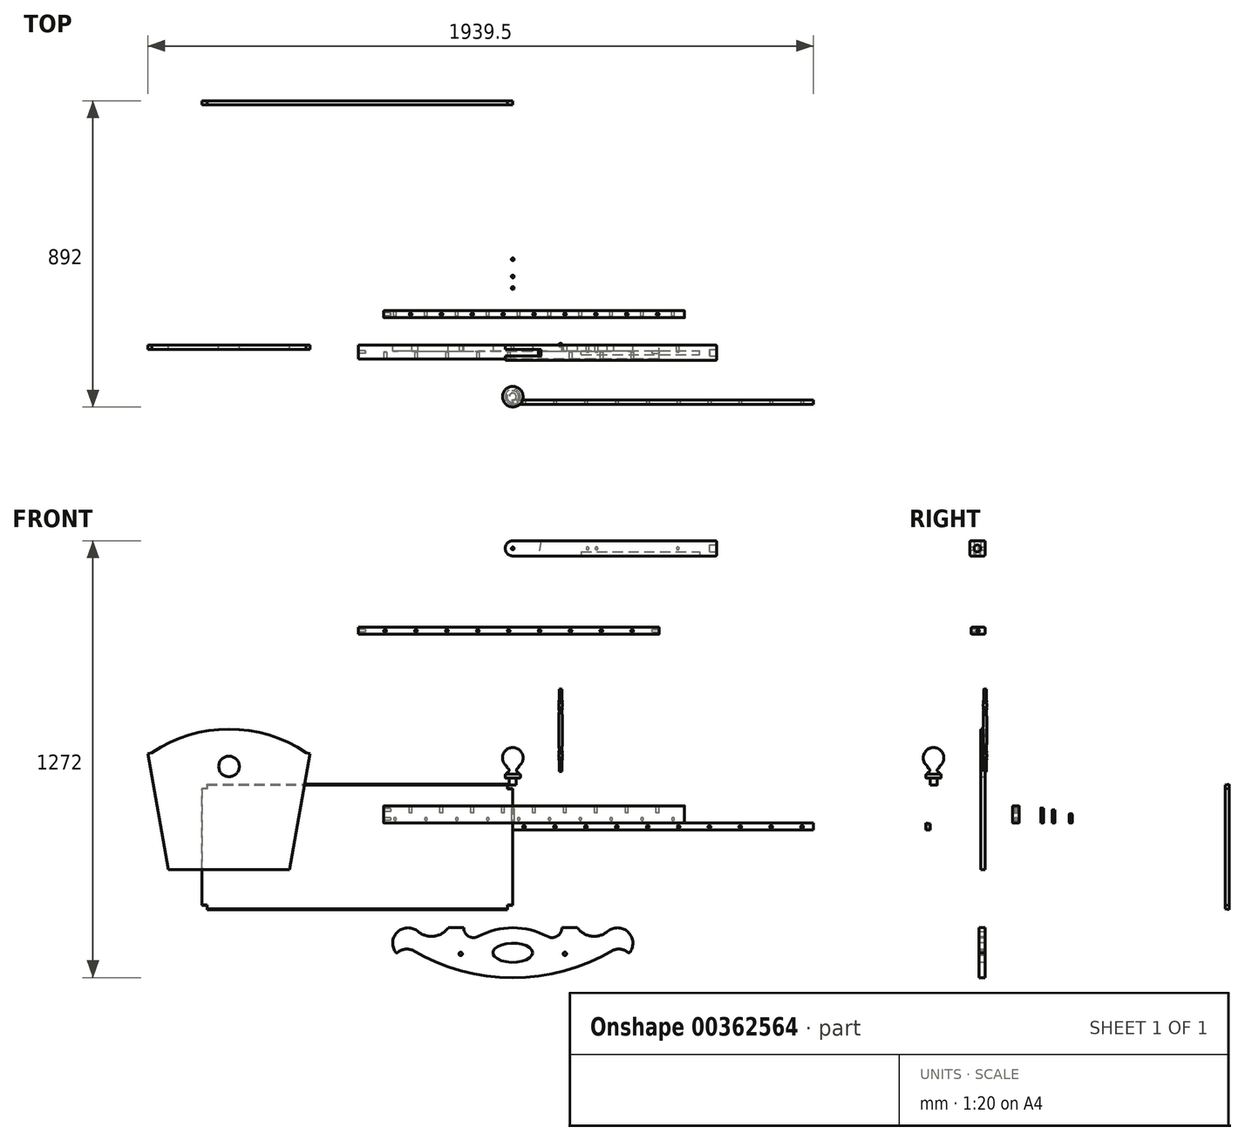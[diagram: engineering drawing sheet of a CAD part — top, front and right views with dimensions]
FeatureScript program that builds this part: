
annotation { "Feature Type Name" : "Feature", "Feature Type Description" : "" }
export const myFeature = defineFeature(function(context is Context, id is Id, definition is map)
    precondition{}
    {
        {
            var Q0;
            Q0=qCreatedBy(makeId("Top.planeOp"),FACE);
            var sketch = newSketch(context, id + "F0", { "sketchPlane" : qUnion([Q0])});
            skLineSegment(sketch, "E0.bottom", {"start": v(-376, 100) * mm, "end": v(500, 100) * mm});
            skLineSegment(sketch, "E0.top", {"start": v(-376, 80) * mm, "end": v(500, 80) * mm});
            skLineSegment(sketch, "E0.left", {"start": v(-376, 100) * mm, "end": v(-376, 80) * mm});
            skLineSegment(sketch, "E0.right", {"start": v(500, 100) * mm, "end": v(500, 80) * mm});
            skSolve(sketch);
        }
        {
            var Q0;
            Q0=makeQuery(id+"F0.imprint","IMPRINT",FACE,{"disambiguationData":[TD([[makeQuery(id+"F0.imprint","IMPRINT",EDGE,{"derivedFrom":sQuery(id+"F0.wireOp",EDGE,"E0.bottom")}),-1.0]])]});
            extrude(context, id + "F1", {"entities" : qUnion([Q0]), "depth" : 50 * mm});
        }
        {
            var Q0;
            Q0=makeQuery(id+"F1.opExtrude","SWEPT_FACE",FACE,{"disambiguationData":[OSD([sQuery(id+"F0.wireOp",EDGE,"E0.left")])]});
            var sketch = newSketch(context, id + "F2", { "sketchPlane" : qUnion([Q0])});
            skCircle(sketch, "E1", {"center": v(-90, 38) * mm, "radius": 4 * mm});
            skLineSegment(sketch, "E2", {"start": v(-90, 50) * mm, "end": v(-90, 0) * mm, "construction": true});
            skLineSegment(sketch, "E3", {"start": v(-100, 38) * mm, "end": v(-80, 38) * mm, "construction": true});
            skLineSegment(sketch, "E4", {"start": v(-100, 12) * mm, "end": v(-80, 12) * mm, "construction": true});
            skLineSegment(sketch, "E5", {"start": v(-100, 25) * mm, "end": v(-80, 25) * mm, "construction": true});
            skCircle(sketch, "E6", {"center": v(-90, 12) * mm, "radius": 4 * mm});
            skSolve(sketch);
        }
        {
            var Q0;
            Q0=makeQuery(id+"F2.imprint","IMPRINT",FACE,{"disambiguationData":[TD([[makeQuery(id+"F2.imprint","IMPRINT",EDGE,{"derivedFrom":sQuery(id+"F2.wireOp",EDGE,"E1")}),-1.0]])]});
            cPlane(context, id + "F3", {"entities" : qUnion([Q0]), "cplaneType" : CPlaneType.OFFSET, "offset" : 438 * mm, "oppositeDirection" : true, "width" : 150 * mm, "height" : 150 * mm});
        }
        {
            var Q0;
            Q0=makeQuery(id+"F2.imprint","IMPRINT",FACE,{"disambiguationData":[TD([[makeQuery(id+"F2.imprint","IMPRINT",EDGE,{"derivedFrom":sQuery(id+"F2.wireOp",EDGE,"E1")}),1.0]])]});
            var Q1;
            Q1=makeQuery(id+"F2.imprint","IMPRINT",FACE,{"disambiguationData":[TD([[makeQuery(id+"F2.imprint","IMPRINT",EDGE,{"derivedFrom":sQuery(id+"F2.wireOp",EDGE,"E6")}),1.0]])]});
            extrude(context, id + "F4", {"entities" : qUnion([Q0, Q1]), "operationType" : NewBodyOperationType.REMOVE, "oppositeDirection" : true, "depth" : 20 * mm});
        }
        {
            var Q0;
            Q0=makeQuery(id+"F1.opExtrude","CAP_FACE",FACE,{"disambiguationData":[OSD([sQuery(id+"F0.wireOp",EDGE,"E0.bottom"),sQuery(id+"F0.wireOp",EDGE,"E0.top"),sQuery(id+"F0.wireOp",EDGE,"E0.left"),sQuery(id+"F0.wireOp",EDGE,"E0.right")])],"isStart":false});
            var sketch = newSketch(context, id + "F5", { "sketchPlane" : qUnion([Q0])});
            skLineSegment(sketch, "E7", {"start": v(500, 90) * mm, "end": v(-376, 90) * mm, "construction": true});
            skCircle(sketch, "E8", {"center": v(-298, 90) * mm, "radius": 4 * mm});
            skCircle(sketch, "E9", {"center": v(-208, 90) * mm, "radius": 4 * mm});
            skCircle(sketch, "E10", {"center": v(-118, 90) * mm, "radius": 4 * mm});
            skCircle(sketch, "E11", {"center": v(-28, 90) * mm, "radius": 4 * mm});
            skCircle(sketch, "E12", {"center": v(62, 90) * mm, "radius": 4 * mm});
            skCircle(sketch, "E13", {"center": v(152, 90) * mm, "radius": 4 * mm});
            skCircle(sketch, "E14", {"center": v(242, 90) * mm, "radius": 4 * mm});
            skCircle(sketch, "E15", {"center": v(332, 90) * mm, "radius": 4 * mm});
            skCircle(sketch, "E16", {"center": v(422, 90) * mm, "radius": 4 * mm});
            skSolve(sketch);
        }
        {
            var Q0;
            Q0=makeQuery(id+"F5.imprint","IMPRINT",FACE,{"disambiguationData":[TD([[makeQuery(id+"F5.imprint","IMPRINT",EDGE,{"derivedFrom":sQuery(id+"F5.wireOp",EDGE,"E8")}),1.0]])]});
            var Q1;
            Q1=makeQuery(id+"F5.imprint","IMPRINT",FACE,{"disambiguationData":[TD([[makeQuery(id+"F5.imprint","IMPRINT",EDGE,{"derivedFrom":sQuery(id+"F5.wireOp",EDGE,"E9")}),1.0]])]});
            var Q2;
            Q2=makeQuery(id+"F5.imprint","IMPRINT",FACE,{"disambiguationData":[TD([[makeQuery(id+"F5.imprint","IMPRINT",EDGE,{"derivedFrom":sQuery(id+"F5.wireOp",EDGE,"E10")}),1.0]])]});
            var Q3;
            Q3=makeQuery(id+"F5.imprint","IMPRINT",FACE,{"disambiguationData":[TD([[makeQuery(id+"F5.imprint","IMPRINT",EDGE,{"derivedFrom":sQuery(id+"F5.wireOp",EDGE,"E11")}),1.0]])]});
            var Q4;
            Q4=makeQuery(id+"F5.imprint","IMPRINT",FACE,{"disambiguationData":[TD([[makeQuery(id+"F5.imprint","IMPRINT",EDGE,{"derivedFrom":sQuery(id+"F5.wireOp",EDGE,"E12")}),1.0]])]});
            var Q5;
            Q5=makeQuery(id+"F5.imprint","IMPRINT",FACE,{"disambiguationData":[TD([[makeQuery(id+"F5.imprint","IMPRINT",EDGE,{"derivedFrom":sQuery(id+"F5.wireOp",EDGE,"E13")}),1.0]])]});
            var Q6;
            Q6=makeQuery(id+"F5.imprint","IMPRINT",FACE,{"disambiguationData":[TD([[makeQuery(id+"F5.imprint","IMPRINT",EDGE,{"derivedFrom":sQuery(id+"F5.wireOp",EDGE,"E14")}),1.0]])]});
            var Q7;
            Q7=makeQuery(id+"F5.imprint","IMPRINT",FACE,{"disambiguationData":[TD([[makeQuery(id+"F5.imprint","IMPRINT",EDGE,{"derivedFrom":sQuery(id+"F5.wireOp",EDGE,"E15")}),1.0]])]});
            var Q8;
            Q8=makeQuery(id+"F5.imprint","IMPRINT",FACE,{"disambiguationData":[TD([[makeQuery(id+"F5.imprint","IMPRINT",EDGE,{"derivedFrom":sQuery(id+"F5.wireOp",EDGE,"E16")}),1.0]])]});
            extrude(context, id + "F6", {"entities" : qUnion([Q0, Q1, Q2, Q3, Q4, Q5, Q6, Q7, Q8]), "operationType" : NewBodyOperationType.REMOVE, "oppositeDirection" : true, "depth" : 20 * mm});
        }
        {
            var Q0;
            Q0=qCreatedBy(makeId("Front.planeOp"),FACE);
            var sketch = newSketch(context, id + "F7", { "sketchPlane" : qUnion([Q0])});
            skLineSegment(sketch, "E17", {"start": v(139.3, 390) * mm, "end": v(139.3, 150) * mm});
            skLineSegment(sketch, "E18", {"start": v(139.3, 150) * mm, "end": v(135.3, 150) * mm});
            skLineSegment(sketch, "E19", {"start": v(135.3, 150) * mm, "end": v(135.3, 170) * mm});
            skLineSegment(sketch, "E20", {"start": v(139.3, 390) * mm, "end": v(135.3, 390) * mm});
            skLineSegment(sketch, "E21", {"start": v(135.3, 390) * mm, "end": v(135.3, 370) * mm});
            skLineSegment(sketch, "E22", {"start": v(135.3, 370) * mm, "end": v(135.3, 358) * mm});
            skArc(sketch, "E23", {"start": v(135.3, 358) * mm, "mid": v(134.27, 354.5) * mm, "end": v(135.3, 351) * mm});
            skArc(sketch, "E24", {"start": v(135.3, 351) * mm, "mid": v(133.83, 343.5) * mm, "end": v(135.3, 336) * mm});
            skArc(sketch, "E25", {"start": v(135.3, 336) * mm, "mid": v(134.27, 332.5) * mm, "end": v(135.3, 329) * mm});
            skLineSegment(sketch, "E26", {"start": v(135.3, 358) * mm, "end": v(139.3, 358) * mm, "construction": true});
            skLineSegment(sketch, "E27", {"start": v(135.3, 351) * mm, "end": v(139.3, 351) * mm, "construction": true});
            skLineSegment(sketch, "E28", {"start": v(135.3, 336) * mm, "end": v(139.3, 336) * mm, "construction": true});
            skLineSegment(sketch, "E29", {"start": v(135.3, 329) * mm, "end": v(139.3, 329) * mm, "construction": true});
            skLineSegment(sketch, "E30", {"start": v(139.3, 270) * mm, "end": v(59.3, 270) * mm, "construction": true});
            skLineSegment(sketch, "E31.MirrorCS", {"start": v(135.3, 211) * mm, "end": v(139.3, 211) * mm, "construction": true});
            skArc(sketch, "E32.MirrorCS", {"start": v(135.3, 204) * mm, "mid": v(134.27, 207.5) * mm, "end": v(135.3, 211) * mm});
            skLineSegment(sketch, "E33.MirrorCS", {"start": v(135.3, 204) * mm, "end": v(139.3, 204) * mm, "construction": true});
            skArc(sketch, "E34.MirrorCS", {"start": v(135.3, 189) * mm, "mid": v(133.83, 196.5) * mm, "end": v(135.3, 204) * mm});
            skLineSegment(sketch, "E35.MirrorCS", {"start": v(135.3, 182) * mm, "end": v(139.3, 182) * mm, "construction": true});
            skLineSegment(sketch, "E36.MirrorCS", {"start": v(135.3, 189) * mm, "end": v(139.3, 189) * mm, "construction": true});
            skArc(sketch, "E37.MirrorCS", {"start": v(135.3, 182) * mm, "mid": v(134.27, 185.5) * mm, "end": v(135.3, 189) * mm});
            skLineSegment(sketch, "E38.MirrorCS", {"start": v(135.3, 170) * mm, "end": v(135.3, 182) * mm});
            skArc(sketch, "E39", {"start": v(135.3, 329) * mm, "mid": v(133.84, 270) * mm, "end": v(135.3, 211) * mm});
            skSolve(sketch);
        }
        {
            var Q0;
            Q0=makeQuery(id+"F7.imprint","IMPRINT",FACE,{"disambiguationData":[TD([[makeQuery(id+"F7.imprint","IMPRINT",EDGE,{"derivedFrom":sQuery(id+"F7.wireOp",EDGE,"E17")}),-1.0]])]});
            var Q1;
            Q1=sQuery(id+"F7.wireOp",EDGE,"E17");
            revolve(context, id + "F8", {"entities" : qUnion([Q0]), "axis" : qUnion([Q1]), "revolveType" : RevolveType.FULL});
        }
        {
            var Q0;
            Q0=qCreatedBy(makeId("Right.planeOp"),FACE);
            var sketch = newSketch(context, id + "F9", { "sketchPlane" : qUnion([Q0])});
            skLineSegment(sketch, "E40", {"start": v(-150, 220) * mm, "end": v(-150, 100) * mm, "construction": true});
            skLineSegment(sketch, "E41", {"start": v(-150, 220) * mm, "end": v(-150, 110.72) * mm});
            skArc(sketch, "E42", {"start": v(-150, 220) * mm, "mid": v(-178.65, 198.9) * mm, "end": v(-167, 165.28) * mm});
            skLineSegment(sketch, "E43", {"start": v(-150, 110.72) * mm, "end": v(-160, 110.72) * mm});
            skLineSegment(sketch, "E44", {"start": v(-160, 110.72) * mm, "end": v(-160, 130.72) * mm});
            skLineSegment(sketch, "E45", {"start": v(-167, 160.28) * mm, "end": v(-167, 165.28) * mm});
            skPoint(sketch, "E46", {"position": v(-167, 154) * mm});
            skArc(sketch, "E47", {"start": v(-167, 147.72) * mm, "mid": v(-160.72, 154) * mm, "end": v(-167, 160.28) * mm});
            skLineSegment(sketch, "E48", {"start": v(-167, 147.72) * mm, "end": v(-167, 142.72) * mm});
            skLineSegment(sketch, "E49", {"start": v(-167, 142.72) * mm, "end": v(-172, 142.72) * mm});
            skLineSegment(sketch, "E50", {"start": v(-172, 142.72) * mm, "end": v(-172, 130.72) * mm});
            skLineSegment(sketch, "E51", {"start": v(-172, 130.72) * mm, "end": v(-160, 130.72) * mm});
            skSolve(sketch);
        }
        {
            var Q0;
            Q0=makeQuery(id+"F9.imprint","IMPRINT",FACE,{"disambiguationData":[TD([[makeQuery(id+"F9.imprint","IMPRINT",EDGE,{"derivedFrom":sQuery(id+"F9.wireOp",EDGE,"E41")}),-1.0]])]});
            var Q1;
            Q1=sQuery(id+"F9.wireOp",EDGE,"E41");
            revolve(context, id + "F10", {"entities" : qUnion([Q0]), "axis" : qUnion([Q1]), "revolveType" : RevolveType.FULL});
        }
        {
            var Q0;
            Q0=qCreatedBy(makeId("Front.planeOp"),FACE);
            var sketch = newSketch(context, id + "F11", { "sketchPlane" : qUnion([Q0])});
            skLineSegment(sketch, "E52", {"start": v(0, -250) * mm, "end": v(0, -450) * mm, "construction": true});
            skArc(sketch, "E53", {"start": v(-275.48, -316.04) * mm, "mid": v(-337.05, -318.41) * mm, "end": v(-338.53, -380.02) * mm});
            skArc(sketch, "E54", {"start": v(-275.48, -316.04) * mm, "mid": v(-229.47, -329.53) * mm, "end": v(-188.27, -305) * mm});
            skArc(sketch, "E55.trimOffspring", {"start": v(-294.24, -369.82) * mm, "mid": v(-317.97, -368.02) * mm, "end": v(-338.53, -380.02) * mm});
            skLineSegment(sketch, "E56", {"start": v(-188.27, -305) * mm, "end": v(-143, -305) * mm});
            skArc(sketch, "E57", {"start": v(-294.24, -369.82) * mm, "mid": v(-152.48, -429.6) * mm, "end": v(0, -450) * mm});
            skArc(sketch, "E58", {"start": v(-143, -305) * mm, "mid": v(-129.19, -329.42) * mm, "end": v(-101.14, -330.17) * mm});
            skArc(sketch, "E59", {"start": v(0, -305) * mm, "mid": v(-52.11, -311.39) * mm, "end": v(-101.14, -330.17) * mm});
            skLineSegment(sketch, "E60.MirrorCS", {"start": v(188.27, -305) * mm, "end": v(143, -305) * mm});
            skArc(sketch, "E61.MirrorCS", {"start": v(294.24, -369.82) * mm, "mid": v(152.48, -429.6) * mm, "end": v(0, -450) * mm});
            skArc(sketch, "E62.MirrorCS", {"start": v(0, -305) * mm, "mid": v(52.11, -311.39) * mm, "end": v(101.14, -330.17) * mm});
            skArc(sketch, "E63.MirrorCS", {"start": v(294.24, -369.82) * mm, "mid": v(317.97, -368.02) * mm, "end": v(338.53, -380.02) * mm});
            skArc(sketch, "E64.MirrorCS", {"start": v(143, -305) * mm, "mid": v(129.19, -329.42) * mm, "end": v(101.14, -330.17) * mm});
            skArc(sketch, "E65.MirrorCS", {"start": v(275.48, -316.04) * mm, "mid": v(229.47, -329.53) * mm, "end": v(188.27, -305) * mm});
            skArc(sketch, "E66.MirrorCS", {"start": v(275.48, -316.04) * mm, "mid": v(337.05, -318.41) * mm, "end": v(338.53, -380.02) * mm});
            skSolve(sketch);
        }
        {
            var Q0;
            Q0=makeQuery(id+"F11.imprint","IMPRINT",FACE,{"disambiguationData":[TD([[makeQuery(id+"F11.imprint","IMPRINT",EDGE,{"derivedFrom":sQuery(id+"F11.wireOp",EDGE,"E53")}),1.0]])]});
            extrude(context, id + "F12", {"entities" : qUnion([Q0]), "depth" : 18 * mm});
        }
        {
            var Q0;
            Q0=makeQuery(id+"F12.opExtrude","SWEPT_EDGE",EDGE,{"disambiguationData":[OSD([sQuery(id+"F11.wireOp",EDGE,"E53"),sQuery(id+"F11.wireOp",EDGE,"E55.trimOffspring")])]});
            var Q1;
            Q1=makeQuery(id+"F12.opExtrude","SWEPT_EDGE",EDGE,{"disambiguationData":[OSD([sQuery(id+"F11.wireOp",EDGE,"E63.MirrorCS"),sQuery(id+"F11.wireOp",EDGE,"E66.MirrorCS")])]});
            fillet(context, id + "F13", {"entities" : qUnion([Q0, Q1]), "radius" : 5 * mm, "tangentPropagation" : true, "allowEdgeOverflow" : false});
        }
        {
            var Q0;
            Q0=makeQuery(id+"F12.opExtrude","CAP_FACE",FACE,{"disambiguationData":[OSD([sQuery(id+"F11.wireOp",EDGE,"E53"),sQuery(id+"F11.wireOp",EDGE,"E54"),sQuery(id+"F11.wireOp",EDGE,"E55.trimOffspring"),sQuery(id+"F11.wireOp",EDGE,"E56"),sQuery(id+"F11.wireOp",EDGE,"E57"),sQuery(id+"F11.wireOp",EDGE,"E58"),sQuery(id+"F11.wireOp",EDGE,"E59"),sQuery(id+"F11.wireOp",EDGE,"E60.MirrorCS"),sQuery(id+"F11.wireOp",EDGE,"E61.MirrorCS"),sQuery(id+"F11.wireOp",EDGE,"E62.MirrorCS"),sQuery(id+"F11.wireOp",EDGE,"E63.MirrorCS"),sQuery(id+"F11.wireOp",EDGE,"E64.MirrorCS"),sQuery(id+"F11.wireOp",EDGE,"E65.MirrorCS"),sQuery(id+"F11.wireOp",EDGE,"E66.MirrorCS")])],"isStart":false});
            var sketch = newSketch(context, id + "F14", { "sketchPlane" : qUnion([Q0])});
            skEllipse(sketch, "E67", {"center": v(0, -377.5) * mm, "majorRadius": 58 * mm, "minorRadius": 28 * mm, "majorAxis": v(1, 0)});
            skLineSegment(sketch, "E68", {"start": v(0, -305) * mm, "end": v(0, -450) * mm, "construction": true});
            skLineSegment(sketch, "E69", {"start": v(-58, -377.5) * mm, "end": v(58, -377.5) * mm, "construction": true});
            skCircle(sketch, "E70", {"center": v(-151.88, -381) * mm, "radius": 5 * mm});
            skCircle(sketch, "E71", {"center": v(151.88, -381) * mm, "radius": 5 * mm});
            skLineSegment(sketch, "E72", {"start": v(-151.88, -381) * mm, "end": v(151.88, -381) * mm, "construction": true});
            skSolve(sketch);
        }
        {
            var Q0;
            Q0=makeQuery(id+"F14.imprint","IMPRINT",FACE,{"disambiguationData":[TD([[makeQuery(id+"F14.imprint","IMPRINT",EDGE,{"derivedFrom":sQuery(id+"F14.wireOp",EDGE,"E70")}),1.0]])]});
            var Q1;
            Q1=makeQuery(id+"F14.imprint","IMPRINT",FACE,{"disambiguationData":[TD([[makeQuery(id+"F14.imprint","IMPRINT",EDGE,{"derivedFrom":sQuery(id+"F14.wireOp",EDGE,"E67")}),1.0]])]});
            var Q2;
            Q2=makeQuery(id+"F14.imprint","IMPRINT",FACE,{"disambiguationData":[TD([[makeQuery(id+"F14.imprint","IMPRINT",EDGE,{"derivedFrom":sQuery(id+"F14.wireOp",EDGE,"E71")}),1.0]])]});
            extrude(context, id + "F15", {"entities" : qUnion([Q0, Q1, Q2]), "operationType" : NewBodyOperationType.REMOVE, "endBound" : BoundingType.UP_TO_NEXT, "oppositeDirection" : true, "depth" : 25 * mm});
        }
        {
            var Q0;
            Q0=qCreatedBy(makeId("Front.planeOp"),FACE);
            var sketch = newSketch(context, id + "F16", { "sketchPlane" : qUnion([Q0])});
            skLineSegment(sketch, "E73", {"start": v(-650, -135) * mm, "end": v(-1004, -135) * mm});
            skLineSegment(sketch, "E74", {"start": v(-1004, -135) * mm, "end": v(-1063.5, 202.44) * mm});
            skLineSegment(sketch, "E75", {"start": v(-650, -135) * mm, "end": v(-590.5, 202.44) * mm});
            skLineSegment(sketch, "E76", {"start": v(-1063.5, 202.44) * mm, "end": v(-1051.68, 204.53) * mm});
            skLineSegment(sketch, "E77", {"start": v(-590.5, 202.44) * mm, "end": v(-602.32, 204.53) * mm});
            skArc(sketch, "E78", {"start": v(-602.32, 204.53) * mm, "mid": v(-827, 273.6) * mm, "end": v(-1051.68, 204.53) * mm});
            skLineSegment(sketch, "E79", {"start": v(-827, 273.6) * mm, "end": v(-827, -135) * mm, "construction": true});
            skCircle(sketch, "E80", {"center": v(-827, 165) * mm, "radius": 30 * mm});
            skSolve(sketch);
        }
        {
            var Q0;
            Q0=makeQuery(id+"F16.imprint","IMPRINT",FACE,{"disambiguationData":[TD([[makeQuery(id+"F16.imprint","IMPRINT",EDGE,{"derivedFrom":sQuery(id+"F16.wireOp",EDGE,"E73")}),-1.0]])]});
            extrude(context, id + "F17", {"entities" : qUnion([Q0]), "depth" : 12 * mm});
        }
        {
            var Q0;
            Q0=qCreatedBy(makeId("Front.planeOp"),FACE);
            var sketch = newSketch(context, id + "F18", { "sketchPlane" : qUnion([Q0])});
            skLineSegment(sketch, "E81", {"start": v(-450, 570) * mm, "end": v(426, 570) * mm});
            skLineSegment(sketch, "E82", {"start": v(426, 570) * mm, "end": v(426, 550) * mm});
            skLineSegment(sketch, "E83", {"start": v(426, 550) * mm, "end": v(-450, 550) * mm});
            skLineSegment(sketch, "E84", {"start": v(-450, 550) * mm, "end": v(-450, 570) * mm});
            skSolve(sketch);
        }
        {
            var Q0;
            Q0=makeQuery(id+"F18.imprint","IMPRINT",FACE,{"disambiguationData":[TD([[makeQuery(id+"F18.imprint","IMPRINT",EDGE,{"derivedFrom":sQuery(id+"F18.wireOp",EDGE,"E81")}),-1.0]])]});
            extrude(context, id + "F19", {"entities" : qUnion([Q0]), "depth" : 40 * mm});
        }
        {
            var Q0;
            Q0=makeQuery(id+"F19.opExtrude","CAP_FACE",FACE,{"disambiguationData":[OSD([sQuery(id+"F18.wireOp",EDGE,"E81"),sQuery(id+"F18.wireOp",EDGE,"E82"),sQuery(id+"F18.wireOp",EDGE,"E83"),sQuery(id+"F18.wireOp",EDGE,"E84")])],"isStart":false});
            var sketch = newSketch(context, id + "F20", { "sketchPlane" : qUnion([Q0])});
            skLineSegment(sketch, "E85", {"start": v(-450, 560) * mm, "end": v(426, 560) * mm, "construction": true});
            skCircle(sketch, "E86", {"center": v(348, 560) * mm, "radius": 4 * mm});
            skCircle(sketch, "E87", {"center": v(258, 560) * mm, "radius": 4 * mm});
            skCircle(sketch, "E88", {"center": v(168, 560) * mm, "radius": 4 * mm});
            skCircle(sketch, "E89", {"center": v(78, 560) * mm, "radius": 4 * mm});
            skCircle(sketch, "E90", {"center": v(-12, 560) * mm, "radius": 4 * mm});
            skCircle(sketch, "E91", {"center": v(-102, 560) * mm, "radius": 4 * mm});
            skCircle(sketch, "E92", {"center": v(-192, 560) * mm, "radius": 4 * mm});
            skCircle(sketch, "E93", {"center": v(-282, 560) * mm, "radius": 4 * mm});
            skCircle(sketch, "E94", {"center": v(-372, 560) * mm, "radius": 4 * mm});
            skSolve(sketch);
        }
        {
            var Q0;
            Q0=makeQuery(id+"F20.imprint","IMPRINT",FACE,{"disambiguationData":[TD([[makeQuery(id+"F20.imprint","IMPRINT",EDGE,{"derivedFrom":sQuery(id+"F20.wireOp",EDGE,"E94")}),1.0]])]});
            var Q1;
            Q1=makeQuery(id+"F20.imprint","IMPRINT",FACE,{"disambiguationData":[TD([[makeQuery(id+"F20.imprint","IMPRINT",EDGE,{"derivedFrom":sQuery(id+"F20.wireOp",EDGE,"E93")}),1.0]])]});
            var Q2;
            Q2=makeQuery(id+"F20.imprint","IMPRINT",FACE,{"disambiguationData":[TD([[makeQuery(id+"F20.imprint","IMPRINT",EDGE,{"derivedFrom":sQuery(id+"F20.wireOp",EDGE,"E92")}),1.0]])]});
            var Q3;
            Q3=makeQuery(id+"F20.imprint","IMPRINT",FACE,{"disambiguationData":[TD([[makeQuery(id+"F20.imprint","IMPRINT",EDGE,{"derivedFrom":sQuery(id+"F20.wireOp",EDGE,"E91")}),1.0]])]});
            var Q4;
            Q4=makeQuery(id+"F20.imprint","IMPRINT",FACE,{"disambiguationData":[TD([[makeQuery(id+"F20.imprint","IMPRINT",EDGE,{"derivedFrom":sQuery(id+"F20.wireOp",EDGE,"E90")}),1.0]])]});
            var Q5;
            Q5=makeQuery(id+"F20.imprint","IMPRINT",FACE,{"disambiguationData":[TD([[makeQuery(id+"F20.imprint","IMPRINT",EDGE,{"derivedFrom":sQuery(id+"F20.wireOp",EDGE,"E89")}),1.0]])]});
            var Q6;
            Q6=makeQuery(id+"F20.imprint","IMPRINT",FACE,{"disambiguationData":[TD([[makeQuery(id+"F20.imprint","IMPRINT",EDGE,{"derivedFrom":sQuery(id+"F20.wireOp",EDGE,"E88")}),1.0]])]});
            var Q7;
            Q7=makeQuery(id+"F20.imprint","IMPRINT",FACE,{"disambiguationData":[TD([[makeQuery(id+"F20.imprint","IMPRINT",EDGE,{"derivedFrom":sQuery(id+"F20.wireOp",EDGE,"E86")}),1.0]])]});
            var Q8;
            Q8=makeQuery(id+"F20.imprint","IMPRINT",FACE,{"disambiguationData":[TD([[makeQuery(id+"F20.imprint","IMPRINT",EDGE,{"derivedFrom":sQuery(id+"F20.wireOp",EDGE,"E87")}),1.0]])]});
            extrude(context, id + "F21", {"entities" : qUnion([Q0, Q1, Q2, Q3, Q4, Q5, Q6, Q7, Q8]), "operationType" : NewBodyOperationType.REMOVE, "oppositeDirection" : true, "depth" : 20 * mm});
        }
        {
            var Q0;
            Q0=makeQuery(id+"F19.opExtrude","SWEPT_FACE",FACE,{"disambiguationData":[OSD([sQuery(id+"F18.wireOp",EDGE,"E82")])]});
            var sketch = newSketch(context, id + "F22", { "sketchPlane" : qUnion([Q0])});
            skLineSegment(sketch, "E95", {"start": v(-20, 570) * mm, "end": v(-20, 550) * mm, "construction": true});
            skLineSegment(sketch, "E96", {"start": v(-40, 560) * mm, "end": v(0, 560) * mm, "construction": true});
            skCircle(sketch, "E97", {"center": v(-20, 560) * mm, "radius": 4 * mm});
            skSolve(sketch);
        }
        {
            var Q0;
            Q0=makeQuery(id+"F22.imprint","IMPRINT",FACE,{"disambiguationData":[TD([[makeQuery(id+"F22.imprint","IMPRINT",EDGE,{"derivedFrom":sQuery(id+"F22.wireOp",EDGE,"E97")}),1.0]])]});
            extrude(context, id + "F23", {"entities" : qUnion([Q0]), "operationType" : NewBodyOperationType.REMOVE, "oppositeDirection" : true, "depth" : 20 * mm});
        }
        {
            var Q0;
            Q0=makeQuery(id+"F19.opExtrude","SWEPT_FACE",FACE,{"disambiguationData":[OSD([sQuery(id+"F18.wireOp",EDGE,"E84")])]});
            var sketch = newSketch(context, id + "F24", { "sketchPlane" : qUnion([Q0])});
            skLineSegment(sketch, "E98", {"start": v(20, 570) * mm, "end": v(20, 550) * mm, "construction": true});
            skLineSegment(sketch, "E99", {"start": v(0, 560) * mm, "end": v(40, 560) * mm, "construction": true});
            skCircle(sketch, "E100", {"center": v(20, 560) * mm, "radius": 4 * mm});
            skSolve(sketch);
        }
        {
            var Q0;
            Q0=makeQuery(id+"F24.imprint","IMPRINT",FACE,{"disambiguationData":[TD([[makeQuery(id+"F24.imprint","IMPRINT",EDGE,{"derivedFrom":sQuery(id+"F24.wireOp",EDGE,"E100")}),1.0]])]});
            extrude(context, id + "F25", {"entities" : qUnion([Q0]), "operationType" : NewBodyOperationType.REMOVE, "oppositeDirection" : true, "depth" : 20 * mm});
        }
        {
            var Q0;
            Q0=makeQuery(id+"F19.opExtrude","CAP_EDGE",EDGE,{"disambiguationData":[OSD([sQuery(id+"F18.wireOp",EDGE,"E83")])],"isStart":false});
            var Q1;
            Q1=makeQuery(id+"F19.opExtrude","CAP_EDGE",EDGE,{"disambiguationData":[OSD([sQuery(id+"F18.wireOp",EDGE,"E83")])],"isStart":true});
            var Q2;
            Q2=makeQuery(id+"F19.opExtrude","CAP_EDGE",EDGE,{"disambiguationData":[OSD([sQuery(id+"F18.wireOp",EDGE,"E81")])],"isStart":false});
            var Q3;
            Q3=makeQuery(id+"F19.opExtrude","CAP_EDGE",EDGE,{"disambiguationData":[OSD([sQuery(id+"F18.wireOp",EDGE,"E81")])],"isStart":true});
            fillet(context, id + "F26", {"entities" : qUnion([Q0, Q1, Q2, Q3]), "radius" : 2 * mm, "tangentPropagation" : true, "allowEdgeOverflow" : false});
        }
        {
            var Q0;
            Q0=makeQuery(id+"F1.opExtrude","CAP_EDGE",EDGE,{"disambiguationData":[OSD([sQuery(id+"F0.wireOp",EDGE,"E0.top")])],"isStart":false});
            var Q1;
            Q1=makeQuery(id+"F1.opExtrude","CAP_EDGE",EDGE,{"disambiguationData":[OSD([sQuery(id+"F0.wireOp",EDGE,"E0.bottom")])],"isStart":false});
            var Q2;
            Q2=makeQuery(id+"F1.opExtrude","CAP_EDGE",EDGE,{"disambiguationData":[OSD([sQuery(id+"F0.wireOp",EDGE,"E0.top")])],"isStart":true});
            var Q3;
            Q3=makeQuery(id+"F1.opExtrude","CAP_EDGE",EDGE,{"disambiguationData":[OSD([sQuery(id+"F0.wireOp",EDGE,"E0.bottom")])],"isStart":true});
            fillet(context, id + "F27", {"entities" : qUnion([Q0, Q1, Q2, Q3]), "radius" : 2 * mm, "tangentPropagation" : true, "allowEdgeOverflow" : false});
        }
        {
            var Q0;
            Q0=makeQuery(id+"F1.opExtrude","SWEPT_FACE",FACE,{"disambiguationData":[OSD([sQuery(id+"F0.wireOp",EDGE,"E0.bottom")])]});
            var sketch = newSketch(context, id + "F28", { "sketchPlane" : qUnion([Q0])});
            skLineSegment(sketch, "E101", {"start": v(-500, 12) * mm, "end": v(376, 12) * mm, "construction": true});
            skCircle(sketch, "E102", {"center": v(-467, 12) * mm, "radius": 4 * mm});
            skCircle(sketch, "E103.1.0.0", {"center": v(-377, 12) * mm, "radius": 4 * mm});
            skCircle(sketch, "E103.2.0.0", {"center": v(-287, 12) * mm, "radius": 4 * mm});
            skCircle(sketch, "E103.3.0.0", {"center": v(-197, 12) * mm, "radius": 4 * mm});
            skCircle(sketch, "E103.4.0.0", {"center": v(-107, 12) * mm, "radius": 4 * mm});
            skCircle(sketch, "E103.5.0.0", {"center": v(-17, 12) * mm, "radius": 4 * mm});
            skCircle(sketch, "E103.6.0.0", {"center": v(73, 12) * mm, "radius": 4 * mm});
            skCircle(sketch, "E103.7.0.0", {"center": v(163, 12) * mm, "radius": 4 * mm});
            skCircle(sketch, "E103.8.0.0", {"center": v(253, 12) * mm, "radius": 4 * mm});
            skCircle(sketch, "E103.9.0.0", {"center": v(343, 12) * mm, "radius": 4 * mm});
            skLineSegment(sketch, "E103.direction1", {"start": v(-467, 12) * mm, "end": v(-377, 12) * mm, "construction": true});
            skSolve(sketch);
        }
        {
            var Q0;
            Q0=makeQuery(id+"F28.imprint","IMPRINT",FACE,{"disambiguationData":[TD([[makeQuery(id+"F28.imprint","IMPRINT",EDGE,{"derivedFrom":sQuery(id+"F28.wireOp",EDGE,"E102")}),1.0]])]});
            var Q1;
            Q1=makeQuery(id+"F28.imprint","IMPRINT",FACE,{"disambiguationData":[TD([[makeQuery(id+"F28.imprint","IMPRINT",EDGE,{"derivedFrom":sQuery(id+"F28.wireOp",EDGE,"E103.1.0.0")}),1.0]])]});
            var Q2;
            Q2=makeQuery(id+"F28.imprint","IMPRINT",FACE,{"disambiguationData":[TD([[makeQuery(id+"F28.imprint","IMPRINT",EDGE,{"derivedFrom":sQuery(id+"F28.wireOp",EDGE,"E103.2.0.0")}),1.0]])]});
            var Q3;
            Q3=makeQuery(id+"F28.imprint","IMPRINT",FACE,{"disambiguationData":[TD([[makeQuery(id+"F28.imprint","IMPRINT",EDGE,{"derivedFrom":sQuery(id+"F28.wireOp",EDGE,"E103.3.0.0")}),1.0]])]});
            var Q4;
            Q4=makeQuery(id+"F28.imprint","IMPRINT",FACE,{"disambiguationData":[TD([[makeQuery(id+"F28.imprint","IMPRINT",EDGE,{"derivedFrom":sQuery(id+"F28.wireOp",EDGE,"E103.4.0.0")}),1.0]])]});
            var Q5;
            Q5=makeQuery(id+"F28.imprint","IMPRINT",FACE,{"disambiguationData":[TD([[makeQuery(id+"F28.imprint","IMPRINT",EDGE,{"derivedFrom":sQuery(id+"F28.wireOp",EDGE,"E103.5.0.0")}),1.0]])]});
            var Q6;
            Q6=makeQuery(id+"F28.imprint","IMPRINT",FACE,{"disambiguationData":[TD([[makeQuery(id+"F28.imprint","IMPRINT",EDGE,{"derivedFrom":sQuery(id+"F28.wireOp",EDGE,"E103.6.0.0")}),1.0]])]});
            var Q7;
            Q7=makeQuery(id+"F28.imprint","IMPRINT",FACE,{"disambiguationData":[TD([[makeQuery(id+"F28.imprint","IMPRINT",EDGE,{"derivedFrom":sQuery(id+"F28.wireOp",EDGE,"E103.7.0.0")}),1.0]])]});
            var Q8;
            Q8=makeQuery(id+"F28.imprint","IMPRINT",FACE,{"disambiguationData":[TD([[makeQuery(id+"F28.imprint","IMPRINT",EDGE,{"derivedFrom":sQuery(id+"F28.wireOp",EDGE,"E103.8.0.0")}),1.0]])]});
            var Q9;
            Q9=makeQuery(id+"F28.imprint","IMPRINT",FACE,{"disambiguationData":[TD([[makeQuery(id+"F28.imprint","IMPRINT",EDGE,{"derivedFrom":sQuery(id+"F28.wireOp",EDGE,"E103.9.0.0")}),1.0]])]});
            extrude(context, id + "F29", {"entities" : qUnion([Q0, Q1, Q2, Q3, Q4, Q5, Q6, Q7, Q8, Q9]), "operationType" : NewBodyOperationType.REMOVE, "oppositeDirection" : true, "depth" : 16 * mm});
        }
        {
            var Q0;
            Q0=makeQuery(id+"F10.opRevolve","SWEPT_EDGE",EDGE,{"disambiguationData":[OSD([sQuery(id+"F9.wireOp",EDGE,"E42"),sQuery(id+"F9.wireOp",EDGE,"E45")])]});
            var Q1;
            Q1=makeQuery(id+"F10.opRevolve","SWEPT_EDGE",EDGE,{"disambiguationData":[OSD([sQuery(id+"F9.wireOp",EDGE,"E45"),sQuery(id+"F9.wireOp",EDGE,"E47")])]});
            var Q2;
            Q2=makeQuery(id+"F10.opRevolve","SWEPT_EDGE",EDGE,{"disambiguationData":[OSD([sQuery(id+"F9.wireOp",EDGE,"E47"),sQuery(id+"F9.wireOp",EDGE,"E48")])]});
            var Q3;
            Q3=makeQuery(id+"F10.opRevolve","SWEPT_EDGE",EDGE,{"disambiguationData":[OSD([sQuery(id+"F9.wireOp",EDGE,"E48"),sQuery(id+"F9.wireOp",EDGE,"E49")])]});
            var Q4;
            Q4=makeQuery(id+"F10.opRevolve","SWEPT_EDGE",EDGE,{"disambiguationData":[OSD([sQuery(id+"F9.wireOp",EDGE,"E49"),sQuery(id+"F9.wireOp",EDGE,"E50")])]});
            var Q5;
            Q5=makeQuery(id+"F10.opRevolve","SWEPT_EDGE",EDGE,{"disambiguationData":[OSD([sQuery(id+"F9.wireOp",EDGE,"E50"),sQuery(id+"F9.wireOp",EDGE,"E51")])]});
            fillet(context, id + "F30", {"entities" : qUnion([Q0, Q1, Q2, Q3, Q4, Q5]), "radius" : 2 * mm, "tangentPropagation" : true, "allowEdgeOverflow" : false});
        }
        {
            var Q0;
            Q0=qCreatedBy(makeId("Top.planeOp"),FACE);
            var sketch = newSketch(context, id + "F31", { "sketchPlane" : qUnion([Q0])});
            skCircle(sketch, "E104", {"center": v(0, 200) * mm, "radius": 4 * mm});
            skSolve(sketch);
        }
        {
            var Q0;
            Q0=makeQuery(id+"F31.imprint","IMPRINT",FACE,{"disambiguationData":[TD([[makeQuery(id+"F31.imprint","IMPRINT",EDGE,{"derivedFrom":sQuery(id+"F31.wireOp",EDGE,"E104")}),1.0]])]});
            var Q1;
            Q1=sQuery(id+"F31.wireOp",EDGE,"E104");
            extrude(context, id + "F32", {"entities" : qUnion([Q0]), "surfaceEntities" : qUnion([Q1]), "depth" : 39 * mm});
        }
        {
            var Q0;
            Q0=makeQuery(id+"F32.opExtrude","CAP_EDGE",EDGE,{"disambiguationData":[OSD([sQuery(id+"F31.wireOp",EDGE,"E104")])],"isStart":false});
            var Q1;
            Q1=makeQuery(id+"F32.opExtrude","CAP_EDGE",EDGE,{"disambiguationData":[OSD([sQuery(id+"F31.wireOp",EDGE,"E104")])],"isStart":true});
            chamfer(context, id + "F33", {"entities" : qUnion([Q0, Q1]), "width" : 0.5 * mm, "tangentPropagation" : true});
        }
        {
            var Q0;
            Q0=qCreatedBy(makeId("Top.planeOp"),FACE);
            var sketch = newSketch(context, id + "F34", { "sketchPlane" : qUnion([Q0])});
            skCircle(sketch, "E105", {"center": v(0, 166.5) * mm, "radius": 4 * mm});
            skSolve(sketch);
        }
        {
            var Q0;
            Q0=makeQuery(id+"F34.imprint","IMPRINT",FACE,{"disambiguationData":[TD([[makeQuery(id+"F34.imprint","IMPRINT",EDGE,{"derivedFrom":sQuery(id+"F34.wireOp",EDGE,"E105")}),1.0]])]});
            extrude(context, id + "F35", {"entities" : qUnion([Q0]), "depth" : 44 * mm});
        }
        {
            var Q0;
            Q0=qCreatedBy(makeId("Front.planeOp"),FACE);
            var sketch = newSketch(context, id + "F36", { "sketchPlane" : qUnion([Q0])});
            skArc(sketch, "E106", {"start": v(0, 822) * mm, "mid": v(-22, 800) * mm, "end": v(0, 778) * mm});
            skLineSegment(sketch, "E107", {"start": v(0, 800) * mm, "end": v(594, 800) * mm, "construction": true});
            skLineSegment(sketch, "E108", {"start": v(0, 822) * mm, "end": v(594, 822) * mm});
            skLineSegment(sketch, "E109", {"start": v(594, 778) * mm, "end": v(0, 778) * mm});
            skLineSegment(sketch, "E110", {"start": v(594, 822) * mm, "end": v(594, 778) * mm});
            skLineSegment(sketch, "E111", {"start": v(0, 800) * mm, "end": v(-22, 800) * mm, "construction": true});
            skSolve(sketch);
        }
        {
            var Q0;
            Q0=makeQuery(id+"F36.imprint","IMPRINT",FACE,{"disambiguationData":[TD([[makeQuery(id+"F36.imprint","IMPRINT",EDGE,{"derivedFrom":sQuery(id+"F36.wireOp",EDGE,"E106")}),1.0]])]});
            extrude(context, id + "F37", {"entities" : qUnion([Q0]), "depth" : 44 * mm});
        }
        {
            var Q0;
            Q0=makeQuery(id+"F37.opExtrude","CAP_FACE",FACE,{"disambiguationData":[OSD([sQuery(id+"F36.wireOp",EDGE,"E106"),sQuery(id+"F36.wireOp",EDGE,"E108"),sQuery(id+"F36.wireOp",EDGE,"E109"),sQuery(id+"F36.wireOp",EDGE,"E110")])],"isStart":true});
            cPlane(context, id + "F38", {"entities" : qUnion([Q0]), "cplaneType" : CPlaneType.OFFSET, "offset" : 13 * mm, "oppositeDirection" : true, "width" : 150 * mm, "height" : 150 * mm});
        }
        {
            var Q0;
            Q0=qCreatedBy(id+"F38.planeOp",FACE);
            var sketch = newSketch(context, id + "F39", { "sketchPlane" : qUnion([Q0])});
            skLineSegment(sketch, "E112", {"start": v(22, 778) * mm, "end": v(22, 822) * mm});
            skLineSegment(sketch, "E113", {"start": v(22, 822) * mm, "end": v(-81.76, 822) * mm});
            skLineSegment(sketch, "E114", {"start": v(-81.76, 822) * mm, "end": v(-74, 778) * mm});
            skLineSegment(sketch, "E115", {"start": v(-74, 778) * mm, "end": v(22, 778) * mm});
            skLineSegment(sketch, "E116", {"start": v(22, 800) * mm, "end": v(-77.88, 800) * mm, "construction": true});
            skSolve(sketch);
        }
        {
            var Q0;
            Q0=makeQuery(id+"F39.imprint","IMPRINT",FACE,{"disambiguationData":[TD([[makeQuery(id+"F39.imprint","IMPRINT",EDGE,{"derivedFrom":sQuery(id+"F39.wireOp",EDGE,"E112")}),1.0]])]});
            extrude(context, id + "F40", {"entities" : qUnion([Q0]), "operationType" : NewBodyOperationType.REMOVE, "oppositeDirection" : true, "depth" : 18 * mm});
        }
        {
            var Q0;
            Q0=makeQuery(id+"F37.opExtrude","CAP_FACE",FACE,{"disambiguationData":[OSD([sQuery(id+"F36.wireOp",EDGE,"E106"),sQuery(id+"F36.wireOp",EDGE,"E108"),sQuery(id+"F36.wireOp",EDGE,"E109"),sQuery(id+"F36.wireOp",EDGE,"E110")])],"isStart":true});
            var sketch = newSketch(context, id + "F41", { "sketchPlane" : qUnion([Q0])});
            skCircle(sketch, "E117", {"center": v(0, 800) * mm, "radius": 4 * mm});
            skLineSegment(sketch, "E118", {"start": v(22, 800) * mm, "end": v(-594, 800) * mm, "construction": true});
            skCircle(sketch, "E119", {"center": v(-481, 800) * mm, "radius": 4 * mm});
            skCircle(sketch, "E120", {"center": v(-244, 800) * mm, "radius": 4 * mm});
            skCircle(sketch, "E121", {"center": v(-218, 800) * mm, "radius": 4 * mm});
            skSolve(sketch);
        }
        {
            var Q0;
            Q0=makeQuery(id+"F41.imprint","IMPRINT",FACE,{"disambiguationData":[TD([[makeQuery(id+"F41.imprint","IMPRINT",EDGE,{"derivedFrom":sQuery(id+"F41.wireOp",EDGE,"E117")}),1.0]])]});
            extrude(context, id + "F42", {"entities" : qUnion([Q0]), "operationType" : NewBodyOperationType.REMOVE, "endBound" : BoundingType.THROUGH_ALL, "oppositeDirection" : true, "depth" : 25 * mm});
        }
        {
            var Q0;
            Q0=makeQuery(id+"F41.imprint","IMPRINT",FACE,{"disambiguationData":[TD([[makeQuery(id+"F41.imprint","IMPRINT",EDGE,{"derivedFrom":sQuery(id+"F41.wireOp",EDGE,"E121")}),1.0]])]});
            var Q1;
            Q1=makeQuery(id+"F41.imprint","IMPRINT",FACE,{"disambiguationData":[TD([[makeQuery(id+"F41.imprint","IMPRINT",EDGE,{"derivedFrom":sQuery(id+"F41.wireOp",EDGE,"E120")}),1.0]])]});
            var Q2;
            Q2=makeQuery(id+"F41.imprint","IMPRINT",FACE,{"disambiguationData":[TD([[makeQuery(id+"F41.imprint","IMPRINT",EDGE,{"derivedFrom":sQuery(id+"F41.wireOp",EDGE,"E119")}),1.0]])]});
            extrude(context, id + "F43", {"entities" : qUnion([Q0, Q1, Q2]), "operationType" : NewBodyOperationType.REMOVE, "oppositeDirection" : true, "depth" : 20 * mm});
        }
        {
            var Q0;
            Q0=makeQuery(id+"F37.opExtrude","SWEPT_FACE",FACE,{"disambiguationData":[OSD([sQuery(id+"F36.wireOp",EDGE,"E109")])]});
            var sketch = newSketch(context, id + "F44", { "sketchPlane" : qUnion([Q0])});
            skLineSegment(sketch, "E122", {"start": v(594, 22) * mm, "end": v(74, 22) * mm, "construction": true});
            skLineSegment(sketch, "E123.bottom", {"start": v(199, 28) * mm, "end": v(544, 28) * mm});
            skLineSegment(sketch, "E123.top", {"start": v(199, 16) * mm, "end": v(544, 16) * mm});
            skLineSegment(sketch, "E123.left", {"start": v(199, 28) * mm, "end": v(199, 16) * mm});
            skLineSegment(sketch, "E123.right", {"start": v(544, 28) * mm, "end": v(544, 16) * mm});
            skSolve(sketch);
        }
        {
            var Q0;
            Q0=makeQuery(id+"F44.imprint","IMPRINT",FACE,{"disambiguationData":[TD([[makeQuery(id+"F44.imprint","IMPRINT",EDGE,{"derivedFrom":sQuery(id+"F44.wireOp",EDGE,"E123.bottom")}),-1.0]])]});
            extrude(context, id + "F45", {"entities" : qUnion([Q0]), "operationType" : NewBodyOperationType.REMOVE, "oppositeDirection" : true, "depth" : 12 * mm});
        }
        {
            var Q0;
            Q0=makeQuery(id+"F37.opExtrude","SWEPT_FACE",FACE,{"disambiguationData":[OSD([sQuery(id+"F36.wireOp",EDGE,"E110")])]});
            var sketch = newSketch(context, id + "F46", { "sketchPlane" : qUnion([Q0])});
            skLineSegment(sketch, "E124", {"start": v(0, 800) * mm, "end": v(-44, 800) * mm, "construction": true});
            skLineSegment(sketch, "E125", {"start": v(-22, 778) * mm, "end": v(-22, 822) * mm, "construction": true});
            skCircle(sketch, "E126", {"center": v(-22, 800) * mm, "radius": 10 * mm});
            skSolve(sketch);
        }
        {
            var Q0;
            Q0 = qSketchRegion(id + "F46", true);
            extrude(context, id + "F47", {"entities" : qUnion([Q0]), "operationType" : NewBodyOperationType.REMOVE, "oppositeDirection" : true, "depth" : 20 * mm});
        }
        {
            var Q0;
            Q0=makeQuery(id+"F37.opExtrude","CAP_EDGE",EDGE,{"disambiguationData":[OSD([sQuery(id+"F36.wireOp",EDGE,"E108")])],"isStart":false});
            var Q1;
            Q1=makeQuery(id+"F37.opExtrude","CAP_EDGE",EDGE,{"disambiguationData":[OSD([sQuery(id+"F36.wireOp",EDGE,"E108")])],"isStart":true});
            var Q2;
            Q2=makeQuery(id+"F37.opExtrude","CAP_EDGE",EDGE,{"disambiguationData":[OSD([sQuery(id+"F36.wireOp",EDGE,"E110")])],"isStart":true});
            var Q3;
            Q3=makeQuery(id+"F37.opExtrude","SWEPT_EDGE",EDGE,{"disambiguationData":[OSD([sQuery(id+"F36.wireOp",EDGE,"E108"),sQuery(id+"F36.wireOp",EDGE,"E110")])]});
            var Q4;
            Q4=makeQuery(id+"F37.opExtrude","CAP_EDGE",EDGE,{"disambiguationData":[OSD([sQuery(id+"F36.wireOp",EDGE,"E110")])],"isStart":false});
            var Q5;
            Q5=makeQuery(id+"F37.opExtrude","SWEPT_EDGE",EDGE,{"disambiguationData":[OSD([sQuery(id+"F36.wireOp",EDGE,"E109"),sQuery(id+"F36.wireOp",EDGE,"E110")])]});
            fillet(context, id + "F48", {"entities" : qUnion([Q0, Q1, Q2, Q3, Q4, Q5]), "radius" : 3 * mm, "tangentPropagation" : true, "allowEdgeOverflow" : false});
        }
        {
            var Q0;
            Q0=qCreatedBy(makeId("Right.planeOp"),FACE);
            var sketch = newSketch(context, id + "F49", { "sketchPlane" : qUnion([Q0])});
            skLineSegment(sketch, "E127", {"start": v(-172, 0) * mm, "end": v(-172, -20) * mm});
            skLineSegment(sketch, "E128", {"start": v(-172, -20) * mm, "end": v(-160, -20) * mm});
            skLineSegment(sketch, "E129", {"start": v(-160, -20) * mm, "end": v(-160, -2.12) * mm});
            skLineSegment(sketch, "E130", {"start": v(-160, -2.12) * mm, "end": v(-172, 0) * mm});
            skSolve(sketch);
        }
        {
            var Q0;
            Q0=makeQuery(id+"F49.imprint","IMPRINT",FACE,{"disambiguationData":[TD([[makeQuery(id+"F49.imprint","IMPRINT",EDGE,{"derivedFrom":sQuery(id+"F49.wireOp",EDGE,"E127")}),1.0]])]});
            extrude(context, id + "F50", {"entities" : qUnion([Q0]), "depth" : 876 * mm});
        }
        {
            var Q0;
            Q0=makeQuery(id+"F50.opExtrude","SWEPT_FACE",FACE,{"disambiguationData":[OSD([sQuery(id+"F49.wireOp",EDGE,"E127")])]});
            var sketch = newSketch(context, id + "F51", { "sketchPlane" : qUnion([Q0])});
            skLineSegment(sketch, "E131", {"start": v(876, -11) * mm, "end": v(0, -11) * mm, "construction": true});
            skCircle(sketch, "E132", {"center": v(843, -11) * mm, "radius": 4 * mm});
            skCircle(sketch, "E133.1.0.0", {"center": v(753, -11) * mm, "radius": 4 * mm});
            skCircle(sketch, "E133.2.0.0", {"center": v(663, -11) * mm, "radius": 4 * mm});
            skCircle(sketch, "E133.3.0.0", {"center": v(573, -11) * mm, "radius": 4 * mm});
            skCircle(sketch, "E133.4.0.0", {"center": v(483, -11) * mm, "radius": 4 * mm});
            skCircle(sketch, "E133.5.0.0", {"center": v(393, -11) * mm, "radius": 4 * mm});
            skCircle(sketch, "E133.6.0.0", {"center": v(303, -11) * mm, "radius": 4 * mm});
            skCircle(sketch, "E133.7.0.0", {"center": v(213, -11) * mm, "radius": 4 * mm});
            skCircle(sketch, "E133.8.0.0", {"center": v(123, -11) * mm, "radius": 4 * mm});
            skCircle(sketch, "E133.9.0.0", {"center": v(33, -11) * mm, "radius": 4 * mm});
            skLineSegment(sketch, "E133.direction1", {"start": v(843, -11) * mm, "end": v(753, -11) * mm, "construction": true});
            skSolve(sketch);
        }
        {
            var Q0;
            Q0=makeQuery(id+"F51.imprint","IMPRINT",FACE,{"disambiguationData":[TD([[makeQuery(id+"F51.imprint","IMPRINT",EDGE,{"derivedFrom":sQuery(id+"F51.wireOp",EDGE,"E133.9.0.0")}),1.0]])]});
            var Q1;
            Q1=makeQuery(id+"F51.imprint","IMPRINT",FACE,{"disambiguationData":[TD([[makeQuery(id+"F51.imprint","IMPRINT",EDGE,{"derivedFrom":sQuery(id+"F51.wireOp",EDGE,"E133.8.0.0")}),1.0]])]});
            var Q2;
            Q2=makeQuery(id+"F51.imprint","IMPRINT",FACE,{"disambiguationData":[TD([[makeQuery(id+"F51.imprint","IMPRINT",EDGE,{"derivedFrom":sQuery(id+"F51.wireOp",EDGE,"E133.7.0.0")}),1.0]])]});
            var Q3;
            Q3=makeQuery(id+"F51.imprint","IMPRINT",FACE,{"disambiguationData":[TD([[makeQuery(id+"F51.imprint","IMPRINT",EDGE,{"derivedFrom":sQuery(id+"F51.wireOp",EDGE,"E133.6.0.0")}),1.0]])]});
            var Q4;
            Q4=makeQuery(id+"F51.imprint","IMPRINT",FACE,{"disambiguationData":[TD([[makeQuery(id+"F51.imprint","IMPRINT",EDGE,{"derivedFrom":sQuery(id+"F51.wireOp",EDGE,"E133.5.0.0")}),1.0]])]});
            var Q5;
            Q5=makeQuery(id+"F51.imprint","IMPRINT",FACE,{"disambiguationData":[TD([[makeQuery(id+"F51.imprint","IMPRINT",EDGE,{"derivedFrom":sQuery(id+"F51.wireOp",EDGE,"E133.4.0.0")}),1.0]])]});
            var Q6;
            Q6=makeQuery(id+"F51.imprint","IMPRINT",FACE,{"disambiguationData":[TD([[makeQuery(id+"F51.imprint","IMPRINT",EDGE,{"derivedFrom":sQuery(id+"F51.wireOp",EDGE,"E133.3.0.0")}),1.0]])]});
            var Q7;
            Q7=makeQuery(id+"F51.imprint","IMPRINT",FACE,{"disambiguationData":[TD([[makeQuery(id+"F51.imprint","IMPRINT",EDGE,{"derivedFrom":sQuery(id+"F51.wireOp",EDGE,"E133.2.0.0")}),1.0]])]});
            var Q8;
            Q8=makeQuery(id+"F51.imprint","IMPRINT",FACE,{"disambiguationData":[TD([[makeQuery(id+"F51.imprint","IMPRINT",EDGE,{"derivedFrom":sQuery(id+"F51.wireOp",EDGE,"E133.1.0.0")}),1.0]])]});
            var Q9;
            Q9=makeQuery(id+"F51.imprint","IMPRINT",FACE,{"disambiguationData":[TD([[makeQuery(id+"F51.imprint","IMPRINT",EDGE,{"derivedFrom":sQuery(id+"F51.wireOp",EDGE,"E132")}),1.0]])]});
            extrude(context, id + "F52", {"entities" : qUnion([Q0, Q1, Q2, Q3, Q4, Q5, Q6, Q7, Q8, Q9]), "operationType" : NewBodyOperationType.REMOVE, "endBound" : BoundingType.UP_TO_NEXT, "oppositeDirection" : true, "depth" : 25 * mm});
        }
        {
            var Q0;
            Q0=qCreatedBy(makeId("Top.planeOp"),FACE);
            var sketch = newSketch(context, id + "F53", { "sketchPlane" : qUnion([Q0])});
            skCircle(sketch, "E134", {"center": v(0, 250) * mm, "radius": 4 * mm});
            skSolve(sketch);
        }
        {
            var Q0;
            Q0=makeQuery(id+"F53.imprint","IMPRINT",FACE,{"disambiguationData":[TD([[makeQuery(id+"F53.imprint","IMPRINT",EDGE,{"derivedFrom":sQuery(id+"F53.wireOp",EDGE,"E134")}),1.0]])]});
            extrude(context, id + "F54", {"entities" : qUnion([Q0]), "depth" : 27 * mm});
        }
        {
            var Q0;
            Q0=makeQuery(id+"F54.opExtrude","CAP_EDGE",EDGE,{"disambiguationData":[OSD([sQuery(id+"F53.wireOp",EDGE,"E134")])],"isStart":false});
            var Q1;
            Q1=makeQuery(id+"F54.opExtrude","CAP_EDGE",EDGE,{"disambiguationData":[OSD([sQuery(id+"F53.wireOp",EDGE,"E134")])],"isStart":true});
            chamfer(context, id + "F55", {"entities" : qUnion([Q0, Q1]), "width" : 1 * mm, "tangentPropagation" : true});
        }
        {
            var Q0;
            Q0=qCreatedBy(makeId("Right.planeOp"),FACE);
            var sketch = newSketch(context, id + "F56", { "sketchPlane" : qUnion([Q0])});
            skLineSegment(sketch, "E135", {"start": v(712, 113.38) * mm, "end": v(712, -252.12) * mm});
            skLineSegment(sketch, "E136", {"start": v(712, -252.12) * mm, "end": v(700, -250) * mm});
            skLineSegment(sketch, "E137", {"start": v(700, -250) * mm, "end": v(700, 111.27) * mm});
            skLineSegment(sketch, "E138", {"start": v(700, 111.27) * mm, "end": v(712, 113.38) * mm});
            skSolve(sketch);
        }
        {
            var Q0;
            Q0=makeQuery(id+"F56.imprint","IMPRINT",FACE,{"disambiguationData":[TD([[makeQuery(id+"F56.imprint","IMPRINT",EDGE,{"derivedFrom":sQuery(id+"F56.wireOp",EDGE,"E135")}),-1.0]])]});
            extrude(context, id + "F57", {"entities" : qUnion([Q0]), "oppositeDirection" : true, "depth" : 906 * mm});
        }
        {
            var Q0;
            Q0=makeQuery(id+"F57.opExtrude","CAP_FACE",FACE,{"disambiguationData":[OSD([sQuery(id+"F56.wireOp",EDGE,"E135"),sQuery(id+"F56.wireOp",EDGE,"E136"),sQuery(id+"F56.wireOp",EDGE,"E137"),sQuery(id+"F56.wireOp",EDGE,"E138")])],"isStart":false});
            var sketch = newSketch(context, id + "F58", { "sketchPlane" : qUnion([Q0])});
            skLineSegment(sketch, "E139", {"start": v(-712, 113.38) * mm, "end": v(-712, 101.2) * mm});
            skLineSegment(sketch, "E140", {"start": v(-712, 101.2) * mm, "end": v(-700, 99.08) * mm});
            skLineSegment(sketch, "E141", {"start": v(-700, 99.08) * mm, "end": v(-700, 111.27) * mm});
            skLineSegment(sketch, "E142", {"start": v(-700, 111.27) * mm, "end": v(-712, 113.38) * mm});
            skLineSegment(sketch, "E143", {"start": v(-712, -252.12) * mm, "end": v(-712, -239.93) * mm});
            skLineSegment(sketch, "E144", {"start": v(-712, -239.93) * mm, "end": v(-700, -237.81) * mm});
            skLineSegment(sketch, "E145", {"start": v(-700, -237.81) * mm, "end": v(-700, -250) * mm});
            skLineSegment(sketch, "E146", {"start": v(-700, -250) * mm, "end": v(-712, -252.12) * mm});
            skSolve(sketch);
        }
        {
            var Q0;
            Q0=makeQuery(id+"F58.imprint","IMPRINT",FACE,{"disambiguationData":[TD([[makeQuery(id+"F58.imprint","IMPRINT",EDGE,{"derivedFrom":sQuery(id+"F58.wireOp",EDGE,"E139")}),1.0]])]});
            var Q1;
            Q1=makeQuery(id+"F58.imprint","IMPRINT",FACE,{"disambiguationData":[TD([[makeQuery(id+"F58.imprint","IMPRINT",EDGE,{"derivedFrom":sQuery(id+"F58.wireOp",EDGE,"E143")}),1.0]])]});
            extrude(context, id + "F59", {"entities" : qUnion([Q0, Q1]), "operationType" : NewBodyOperationType.REMOVE, "oppositeDirection" : true, "depth" : 15 * mm});
        }
        {
            var Q0;
            Q0=makeQuery(id+"F57.opExtrude","CAP_FACE",FACE,{"disambiguationData":[OSD([sQuery(id+"F56.wireOp",EDGE,"E135"),sQuery(id+"F56.wireOp",EDGE,"E136"),sQuery(id+"F56.wireOp",EDGE,"E137"),sQuery(id+"F56.wireOp",EDGE,"E138")])],"isStart":true});
            var sketch = newSketch(context, id + "F60", { "sketchPlane" : qUnion([Q0])});
            skLineSegment(sketch, "E147", {"start": v(700, 111.27) * mm, "end": v(712, 113.38) * mm});
            skLineSegment(sketch, "E148", {"start": v(712, 113.38) * mm, "end": v(712, 101.2) * mm});
            skLineSegment(sketch, "E149", {"start": v(712, 101.2) * mm, "end": v(700, 99.08) * mm});
            skLineSegment(sketch, "E150", {"start": v(700, 99.08) * mm, "end": v(700, 111.27) * mm});
            skLineSegment(sketch, "E151", {"start": v(712, -252.12) * mm, "end": v(712, -239.93) * mm});
            skLineSegment(sketch, "E152", {"start": v(712, -239.93) * mm, "end": v(700, -237.81) * mm});
            skLineSegment(sketch, "E153", {"start": v(700, -237.81) * mm, "end": v(700, -250) * mm});
            skLineSegment(sketch, "E154", {"start": v(700, -250) * mm, "end": v(712, -252.12) * mm});
            skSolve(sketch);
        }
        {
            var Q0;
            Q0=makeQuery(id+"F60.imprint","IMPRINT",FACE,{"disambiguationData":[TD([[makeQuery(id+"F60.imprint","IMPRINT",EDGE,{"derivedFrom":sQuery(id+"F60.wireOp",EDGE,"E147")}),-1.0]])]});
            var Q1;
            Q1=makeQuery(id+"F60.imprint","IMPRINT",FACE,{"disambiguationData":[TD([[makeQuery(id+"F60.imprint","IMPRINT",EDGE,{"derivedFrom":sQuery(id+"F60.wireOp",EDGE,"E151")}),-1.0]])]});
            extrude(context, id + "F61", {"entities" : qUnion([Q0, Q1]), "operationType" : NewBodyOperationType.REMOVE, "oppositeDirection" : true, "depth" : 15 * mm});
        }
    });
